# Revit family: 1990098 - Armonia AMX120
name_source: partatom
category: Plumbing Fixtures
revit_build: Autodesk Revit 2018 (Build: 20170927_1515(x64)
units: mm (PartAtom-declared; Revit-internal decimal feet)

## family parameters
Always vertical = Yes
Cut with Voids When Loaded = No
OmniClass Number = 23.45.05.14.99
OmniClass Title = Other Sanitary Washing Plumbing Fixtures
Part Type = Normal
Room Calculation Point = No
Round Connector Dimension = Use Diameter
Shared = No
Work Plane-Based = No

## types (1)
- Armonia AMX120
    Assembly Code = D2010410
    Bowl Dimensions = 340mm x 400mm x 190mm
    CW Connection = No
    HW Connection = No
    Manufacturer = Franke South Africa (Pty) Ltd
    Material = Austenitic Stainless Steel, Satin finish
    Model = Armonia AMX120
    Product Code = 1990098
    Sink Dimensions = 765mm x 450mm
    Vent Connection = No
    Waste Connection = Yes

## geometry (parser evidence)
native form markers: Blend x8, Sweep x2
no freeform markers — native parametric forms only
